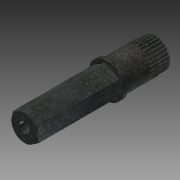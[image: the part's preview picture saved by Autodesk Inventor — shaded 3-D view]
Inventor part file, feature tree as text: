
AUTODESK INVENTOR PART (.ipt)
format: ipt  version: 2014 (Build 180170000, 170)  size: 2,089,984 bytes
history: native  units: in
note: dims shown in document units (in); Inventor stores cm internally (conversion verified against a paired STEP export)
features: fillet x1, imported_body x1
ambient origin geometry x8: Origin, YZ Plane, XZ Plane, XY Plane, X Axis, Y Axis, Z Axis, Center Point
bodies: Body1 (feature_tree)
feature tree (2):
  fillet  "Fillet5"  [1 undecoded]
  imported_body  "Base1"
note: 1 required parameter value undecoded (feature->parameter linkage not recoverable at this tier; creation-order binding heuristic only, values carry confidence <= 0.55)
